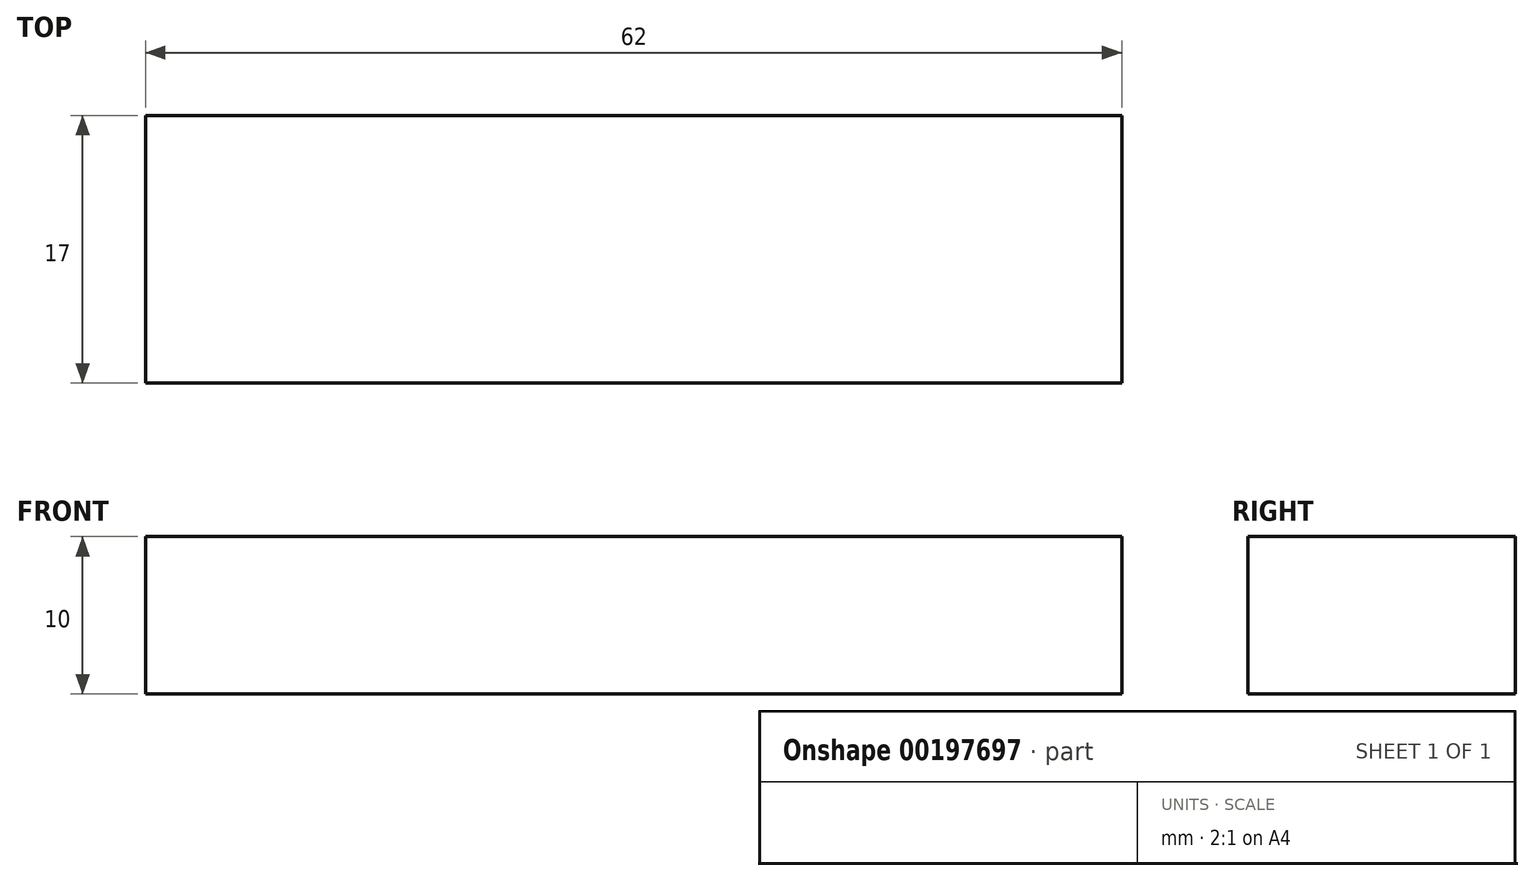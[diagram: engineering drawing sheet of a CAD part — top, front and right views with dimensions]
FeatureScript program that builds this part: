
annotation { "Feature Type Name" : "Feature", "Feature Type Description" : "" }
export const myFeature = defineFeature(function(context is Context, id is Id, definition is map)
    precondition{}
    {
        {
            var Q0;
            Q0=qCreatedBy(makeId("Top.planeOp"),FACE);
            var sketch = newSketch(context, id + "F0", { "sketchPlane" : qUnion([Q0])});
            skLineSegment(sketch, "E0.bottom", {"start": v(31, -8.5) * mm, "end": v(-31, -8.5) * mm});
            skLineSegment(sketch, "E0.top", {"start": v(31, 8.5) * mm, "end": v(-31, 8.5) * mm});
            skLineSegment(sketch, "E0.left", {"start": v(31, -8.5) * mm, "end": v(31, 8.5) * mm});
            skLineSegment(sketch, "E0.right", {"start": v(-31, -8.5) * mm, "end": v(-31, 8.5) * mm});
            skPoint(sketch, "E0.middle", {"position": v(0, 0) * mm});
            skSolve(sketch);
        }
        {
            var Q0;
            Q0 = qSketchRegion(id + "F0", true);
            extrude(context, id + "F1", {"entities" : qUnion([Q0]), "depth" : 10 * mm});
        }
    });
